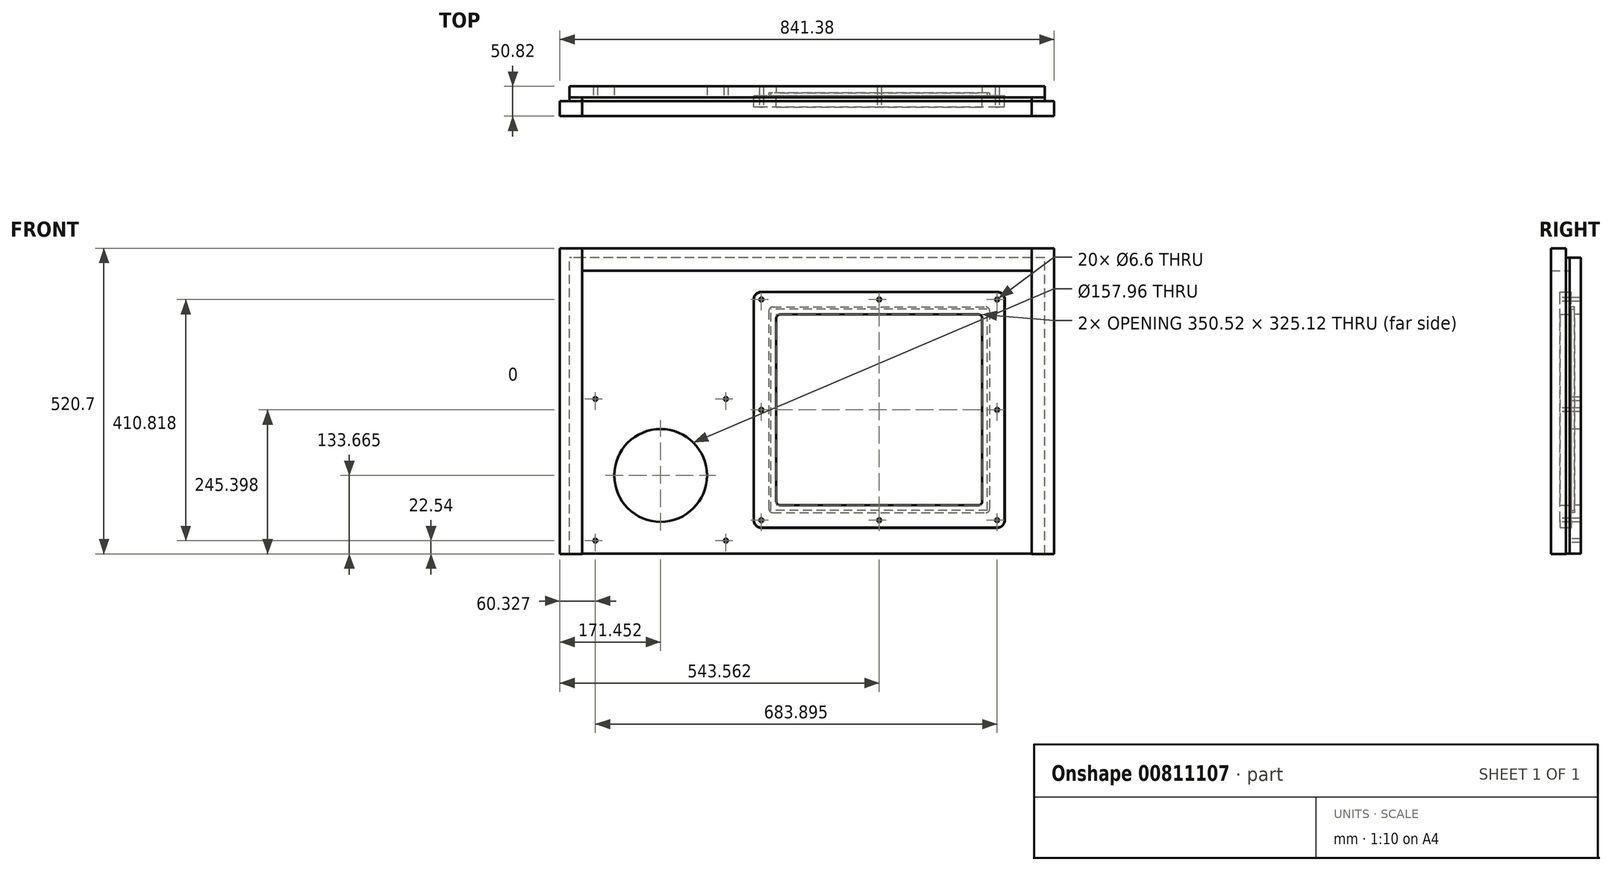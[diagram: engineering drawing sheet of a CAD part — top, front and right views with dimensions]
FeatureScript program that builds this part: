
annotation { "Feature Type Name" : "Feature", "Feature Type Description" : "" }
export const myFeature = defineFeature(function(context is Context, id is Id, definition is map)
    precondition{}
    {
        {
            var Q0;
            Q0=qCreatedBy(makeId("Front.planeOp"),FACE);
            cPlane(context, id + "F0", {"entities" : qUnion([Q0]), "cplaneType" : CPlaneType.OFFSET, "offset" : 25.4 * mm, "width" : 150 * mm, "height" : 150 * mm});
        }
        {
            var Q0;
            Q0=qCreatedBy(makeId("Front.planeOp"),FACE);
            var sketch = newSketch(context, id + "F1", { "sketchPlane" : qUnion([Q0])});
            skLineSegment(sketch, "E0.bottom", {"start": v(406.4, -254) * mm, "end": v(-406.4, -254) * mm});
            skLineSegment(sketch, "E0.top", {"start": v(406.4, 254) * mm, "end": v(-406.4, 254) * mm});
            skLineSegment(sketch, "E0.left", {"start": v(406.4, -254) * mm, "end": v(406.4, 254) * mm});
            skLineSegment(sketch, "E0.right", {"start": v(-406.4, -254) * mm, "end": v(-406.4, 254) * mm});
            skPoint(sketch, "E0.middle", {"position": v(0, 0) * mm});
            skSolve(sketch);
        }
        {
            var Q0;
            Q0=qCreatedBy(id+"F0.planeOp",FACE);
            var sketch = newSketch(context, id + "F2", { "sketchPlane" : qUnion([Q0])});
            skLineSegment(sketch, "E1.bottom", {"start": v(420.69, -252.41) * mm, "end": v(-420.69, -252.41) * mm});
            skLineSegment(sketch, "E1.top", {"start": v(420.69, 268.29) * mm, "end": v(-420.69, 268.29) * mm});
            skLineSegment(sketch, "E1.left", {"start": v(420.69, -252.41) * mm, "end": v(420.69, 268.29) * mm});
            skLineSegment(sketch, "E1.right", {"start": v(-420.69, -252.41) * mm, "end": v(-420.69, 268.29) * mm});
            skPoint(sketch, "E1.middle", {"position": v(0, 7.94) * mm});
            skSolve(sketch);
        }
        {
            var Q0;
            Q0=qCreatedBy(makeId("Front.planeOp"),FACE);
            var sketch = newSketch(context, id + "F3", { "sketchPlane" : qUnion([Q0])});
            skLineSegment(sketch, "E2.bottom", {"start": v(404.5, -252.1) * mm, "end": v(-404.5, -252.1) * mm});
            skLineSegment(sketch, "E2.top", {"start": v(404.5, 252.1) * mm, "end": v(-404.5, 252.1) * mm});
            skLineSegment(sketch, "E2.left", {"start": v(404.5, -252.1) * mm, "end": v(404.5, 252.1) * mm});
            skLineSegment(sketch, "E2.right", {"start": v(-404.5, -252.1) * mm, "end": v(-404.5, 252.1) * mm});
            skPoint(sketch, "E2.middle", {"position": v(0, 0) * mm});
            skLineSegment(sketch, "E3", {"start": v(-404.5, 22.52) * mm, "end": v(-406.4, 22.52) * mm, "construction": true});
            skLineSegment(sketch, "E4", {"start": v(-361.84, 252.1) * mm, "end": v(-361.84, 254) * mm, "construction": true});
            skSolve(sketch);
        }
        {
            var Q0;
            Q0 = qSketchRegion(id + "F3", true);
            extrude(context, id + "F4", {"entities" : qUnion([Q0]), "depth" : 19.05 * mm, "offsetDistance" : 25.4 * mm});
        }
        {
            var Q0;
            Q0=qCreatedBy(id+"F0.planeOp",FACE);
            var sketch = newSketch(context, id + "F5", { "sketchPlane" : qUnion([Q0])});
            skPoint(sketch, "E5", {"position": v(-420.69, 153.57) * mm});
            skLineSegment(sketch, "E6.bottom", {"start": v(-420.69, 268.29) * mm, "end": v(-382.59, 268.29) * mm});
            skLineSegment(sketch, "E6.top", {"start": v(-420.69, -252.41) * mm, "end": v(-382.59, -252.41) * mm});
            skLineSegment(sketch, "E6.left", {"start": v(-420.69, 268.29) * mm, "end": v(-420.69, -252.41) * mm});
            skLineSegment(sketch, "E6.right", {"start": v(-382.59, 268.29) * mm, "end": v(-382.59, -252.41) * mm});
            skLineSegment(sketch, "E7", {"start": v(0, 481.6) * mm, "end": v(0, -396.4) * mm, "construction": true});
            skLineSegment(sketch, "E8.MirrorCS", {"start": v(420.69, -252.41) * mm, "end": v(382.59, -252.41) * mm});
            skLineSegment(sketch, "E9.MirrorCS", {"start": v(382.59, 268.29) * mm, "end": v(382.59, -252.41) * mm});
            skLineSegment(sketch, "E10.MirrorCS", {"start": v(420.69, 268.29) * mm, "end": v(420.69, -252.41) * mm});
            skLineSegment(sketch, "E11.MirrorCS", {"start": v(420.69, 268.29) * mm, "end": v(382.59, 268.29) * mm});
            skPoint(sketch, "E12.MirrorP", {"position": v(420.69, 153.57) * mm});
            skLineSegment(sketch, "E13.bottom", {"start": v(-382.59, 268.29) * mm, "end": v(382.59, 268.29) * mm});
            skLineSegment(sketch, "E13.top", {"start": v(-382.59, 230.19) * mm, "end": v(382.59, 230.19) * mm});
            skLineSegment(sketch, "E13.left", {"start": v(-382.59, 268.29) * mm, "end": v(-382.59, 230.19) * mm});
            skLineSegment(sketch, "E13.right", {"start": v(382.59, 268.29) * mm, "end": v(382.59, 230.19) * mm});
            skSolve(sketch);
        }
        {
            var Q0;
            Q0=makeQuery(id+"F5.imprint","IMPRINT",FACE,{"disambiguationData":[TD([[makeQuery(id+"F5.imprint","IMPRINT",EDGE,{"derivedFrom":sQuery(id+"F5.wireOp",EDGE,"E6.bottom")}),-1.0]])]});
            var Q1;
            Q1=makeQuery(id+"F5.imprint","IMPRINT",FACE,{"disambiguationData":[TD([[makeQuery(id+"F5.imprint","IMPRINT",EDGE,{"derivedFrom":sQuery(id+"F5.wireOp",EDGE,"E8.MirrorCS")}),-1.0]])]});
            extrude(context, id + "F6", {"entities" : qUnion([Q0, Q1]), "depth" : 25.4 * mm + 5 / 203.2 * mm, "offsetDistance" : 25.4 * mm});
        }
        {
            var Q0;
            Q0=makeQuery(id+"F5.imprint","IMPRINT",FACE,{"disambiguationData":[TD([[makeQuery(id+"F5.imprint","IMPRINT",EDGE,{"derivedFrom":sQuery(id+"F5.wireOp",EDGE,"E13.bottom")}),-1.0]])]});
            var Q1;
            Q1=makeQuery(id+"F6.opExtrude","CAP_FACE",FACE,{"disambiguationData":[OSD([sQuery(id+"F5.wireOp",EDGE,"E6.bottom"),sQuery(id+"F5.wireOp",EDGE,"E6.top"),sQuery(id+"F5.wireOp",EDGE,"E6.left"),sQuery(id+"F5.wireOp",EDGE,"E6.right"),sQuery(id+"F5.wireOp",EDGE,"E13.left")])],"isStart":false});
            extrude(context, id + "F7", {"entities" : qUnion([Q0]), "endBound" : BoundingType.UP_TO_SURFACE, "depth" : 25.4 * mm, "endBoundEntityFace" : qUnion([Q1]), "offsetDistance" : 25.4 * mm});
        }
        {
            var Q0;
            Q0=makeQuery(id+"F4.opExtrude","CAP_FACE",FACE,{"disambiguationData":[OSD([sQuery(id+"F3.wireOp",EDGE,"E2.bottom"),sQuery(id+"F3.wireOp",EDGE,"E2.top"),sQuery(id+"F3.wireOp",EDGE,"E2.left"),sQuery(id+"F3.wireOp",EDGE,"E2.right")])],"isStart":false});
            var sketch = newSketch(context, id + "F8", { "sketchPlane" : qUnion([Q0])});
            skLineSegment(sketch, "E14.0", {"start": v(-404.5, -252.1) * mm, "end": v(-404.5, 252.1) * mm, "construction": true});
            skLineSegment(sketch, "E15.0", {"start": v(404.5, 252.1) * mm, "end": v(-404.5, 252.1) * mm, "construction": true});
            skLineSegment(sketch, "E16.0", {"start": v(404.5, -252.1) * mm, "end": v(404.5, 252.1) * mm, "construction": true});
            skLineSegment(sketch, "E17.0", {"start": v(420.69, -252.41) * mm, "end": v(382.59, -252.41) * mm, "construction": true});
            skLineSegment(sketch, "E18.0", {"start": v(382.59, 268.29) * mm, "end": v(382.59, -252.41) * mm, "construction": true});
            skLineSegment(sketch, "E19.0", {"start": v(-382.59, 268.29) * mm, "end": v(-382.59, -252.41) * mm, "construction": true});
            skLineSegment(sketch, "E20.0", {"start": v(-382.59, 230.19) * mm, "end": v(382.59, 230.19) * mm, "construction": true});
            skLineSegment(sketch, "E21.bottom", {"start": v(-404.5, 252.1) * mm, "end": v(-382.59, 252.1) * mm});
            skLineSegment(sketch, "E21.top", {"start": v(-404.5, -252.41) * mm, "end": v(-382.59, -252.41) * mm});
            skLineSegment(sketch, "E21.left", {"start": v(-404.5, 252.1) * mm, "end": v(-404.5, -252.41) * mm});
            skLineSegment(sketch, "E21.right", {"start": v(-382.59, 252.1) * mm, "end": v(-382.59, -252.41) * mm});
            skLineSegment(sketch, "E22.bottom", {"start": v(-382.59, 252.1) * mm, "end": v(382.59, 252.1) * mm});
            skLineSegment(sketch, "E22.top", {"start": v(-382.59, 230.19) * mm, "end": v(382.59, 230.19) * mm});
            skLineSegment(sketch, "E22.left", {"start": v(-382.59, 252.1) * mm, "end": v(-382.59, 230.19) * mm});
            skLineSegment(sketch, "E22.right", {"start": v(382.59, 252.1) * mm, "end": v(382.59, 230.19) * mm});
            skLineSegment(sketch, "E23.bottom", {"start": v(382.59, 252.1) * mm, "end": v(404.5, 252.1) * mm});
            skLineSegment(sketch, "E23.top", {"start": v(382.59, -252.1) * mm, "end": v(404.5, -252.1) * mm});
            skLineSegment(sketch, "E23.left", {"start": v(382.59, 252.1) * mm, "end": v(382.59, -252.1) * mm});
            skLineSegment(sketch, "E23.right", {"start": v(404.5, 252.1) * mm, "end": v(404.5, -252.1) * mm});
            skSolve(sketch);
        }
        {
            var Q0;
            Q0=makeQuery(id+"F8.imprint","IMPRINT",FACE,{"disambiguationData":[TD([[makeQuery(id+"F8.imprint","IMPRINT",EDGE,{"derivedFrom":sQuery(id+"F8.wireOp",EDGE,"E21.bottom")}),1.0]])]});
            var Q1;
            {var subQ3=sQuery(id+"F8.wireOp",EDGE,"E23.bottom");Q1=makeQuery(id+"F8.imprint","IMPRINT",FACE,{"disambiguationData":[TD([[makeQuery(id+"F8.imprint","IMPRINT",EDGE,{"derivedFrom":subQ3}),1.0]])]});}
            var Q2;
            Q2=qCreatedBy(id+"F0.planeOp",FACE);
            extrude(context, id + "F9", {"entities" : qUnion([Q0, Q1]), "endBound" : BoundingType.UP_TO_SURFACE, "depth" : 25.4 * mm, "endBoundEntityFace" : qUnion([Q2]), "offsetDistance" : 25.4 * mm});
        }
        {
            var Q0;
            {var subQ0=sQuery(id+"F8.wireOp",EDGE,"E22.bottom");Q0=makeQuery(id+"F8.imprint","IMPRINT",FACE,{"disambiguationData":[TD([[makeQuery(id+"F8.imprint","IMPRINT",EDGE,{"derivedFrom":subQ0}),1.0]])]});}
            var Q1;
            Q1=qCreatedBy(id+"F0.planeOp",FACE);
            extrude(context, id + "F10", {"entities" : qUnion([Q0]), "endBound" : BoundingType.UP_TO_SURFACE, "depth" : 25.4 * mm, "endBoundEntityFace" : qUnion([Q1]), "offsetDistance" : 25.4 * mm});
        }
        {
            var Q0;
            Q0=makeQuery(id+"F4.opExtrude","CAP_FACE",FACE,{"disambiguationData":[OSD([sQuery(id+"F3.wireOp",EDGE,"E2.bottom"),sQuery(id+"F3.wireOp",EDGE,"E2.top"),sQuery(id+"F3.wireOp",EDGE,"E2.left"),sQuery(id+"F3.wireOp",EDGE,"E2.right")])],"isStart":false});
            var sketch = newSketch(context, id + "F11", { "sketchPlane" : qUnion([Q0])});
            skLineSegment(sketch, "E24", {"start": v(-638.96, -118.75) * mm, "end": v(167.87, -118.75) * mm, "construction": true});
            skLineSegment(sketch, "E25", {"start": v(-249.24, -343.57) * mm, "end": v(-249.24, 396.02) * mm, "construction": true});
            skCircle(sketch, "E26", {"center": v(-249.24, -118.75) * mm, "radius": 77.79 * mm, "construction": true});
            skLineSegment(sketch, "E27.bottom", {"start": v(-369.89, 20.95) * mm, "end": v(-128.59, 20.95) * mm, "construction": true});
            skLineSegment(sketch, "E27.top", {"start": v(-369.89, -239.4) * mm, "end": v(-128.59, -239.4) * mm, "construction": true});
            skLineSegment(sketch, "E27.left", {"start": v(-369.89, 20.95) * mm, "end": v(-369.89, -239.4) * mm, "construction": true});
            skLineSegment(sketch, "E27.right", {"start": v(-128.59, 20.95) * mm, "end": v(-128.59, -239.4) * mm, "construction": true});
            skPoint(sketch, "E28", {"position": v(-249.24, 20.95) * mm});
            skLineSegment(sketch, "E29", {"start": v(-360.36, 91.16) * mm, "end": v(-360.36, -269.14) * mm, "construction": true});
            skLineSegment(sketch, "E30", {"start": v(-374.2, 11.43) * mm, "end": v(-35.6, 11.43) * mm, "construction": true});
            skLineSegment(sketch, "E31", {"start": v(-377.42, -229.87) * mm, "end": v(-85.49, -229.87) * mm, "construction": true});
            skCircle(sketch, "E32", {"center": v(-360.36, -229.87) * mm, "radius": 3.3 * mm});
            skCircle(sketch, "E33", {"center": v(-360.36, 11.43) * mm, "radius": 3.3 * mm});
            skCircle(sketch, "E34.MirrorC", {"center": v(-138.11, -229.87) * mm, "radius": 3.3 * mm});
            skCircle(sketch, "E35.MirrorC", {"center": v(-138.11, 11.43) * mm, "radius": 3.3 * mm});
            skCircle(sketch, "E36", {"center": v(-249.24, -118.75) * mm, "radius": 78.98 * mm});
            skLineSegment(sketch, "E37", {"start": v(-249.24, -118.75) * mm, "end": v(-193.1, -64.9) * mm, "construction": true});
            skLineSegment(sketch, "E38", {"start": v(-193.1, -64.9) * mm, "end": v(-192.24, -64.08) * mm, "construction": true});
            skSolve(sketch);
        }
        {
            var Q0;
            Q0 = qSketchRegion(id + "F11", true);
            extrude(context, id + "F12", {"entities" : qUnion([Q0]), "operationType" : NewBodyOperationType.REMOVE, "endBound" : BoundingType.THROUGH_ALL, "oppositeDirection" : true, "depth" : 25.4 * mm, "offsetDistance" : 25.4 * mm});
        }
        {
            var Q0;
            Q0=makeQuery(id+"F11.imprint","IMPRINT",FACE,{"disambiguationData":[TD([[makeQuery(id+"F11.imprint","IMPRINT",EDGE,{"derivedFrom":sQuery(id+"F11.wireOp",EDGE,"E32")}),-1.0]])]});
            var sketch = newSketch(context, id + "F13", { "sketchPlane" : qUnion([Q0])});
            skLineSegment(sketch, "E39.bottom", {"start": v(304.36, -182.27) * mm, "end": v(-58.61, -182.27) * mm});
            skLineSegment(sketch, "E39.top", {"start": v(304.36, 168.25) * mm, "end": v(-58.61, 168.25) * mm});
            skLineSegment(sketch, "E39.left", {"start": v(310.83, -175.8) * mm, "end": v(310.83, 161.77) * mm});
            skLineSegment(sketch, "E39.right", {"start": v(-65.09, -175.8) * mm, "end": v(-65.09, 161.77) * mm});
            skPoint(sketch, "E39.middle", {"position": v(122.87, -7.01) * mm});
            skPoint(sketch, "E40.visualSharp", {"position": v(-65.09, 168.25) * mm});
            skArc(sketch, "E40.filletArc", {"start": v(-58.61, 168.25) * mm, "mid": v(-63.2, 166.35) * mm, "end": v(-65.09, 161.77) * mm});
            skPoint(sketch, "E41.visualSharp", {"position": v(310.83, 168.25) * mm});
            skArc(sketch, "E41.filletArc", {"start": v(310.83, 161.77) * mm, "mid": v(308.94, 166.35) * mm, "end": v(304.36, 168.25) * mm});
            skPoint(sketch, "E42.visualSharp", {"position": v(310.83, -182.27) * mm});
            skArc(sketch, "E42.filletArc", {"start": v(304.36, -182.27) * mm, "mid": v(308.94, -180.38) * mm, "end": v(310.83, -175.8) * mm});
            skPoint(sketch, "E43.visualSharp", {"position": v(-65.09, -182.27) * mm});
            skArc(sketch, "E43.filletArc", {"start": v(-65.09, -175.8) * mm, "mid": v(-63.2, -180.38) * mm, "end": v(-58.61, -182.27) * mm});
            skLineSegment(sketch, "E44.bottom", {"start": v(307.02, -178.46) * mm, "end": v(-61.28, -178.46) * mm});
            skLineSegment(sketch, "E44.top", {"start": v(307.02, 164.44) * mm, "end": v(-61.28, 164.44) * mm});
            skLineSegment(sketch, "E44.left", {"start": v(307.02, -178.46) * mm, "end": v(307.02, 164.44) * mm});
            skLineSegment(sketch, "E44.right", {"start": v(-61.28, -178.46) * mm, "end": v(-61.28, 164.44) * mm});
            skLineSegment(sketch, "E45", {"start": v(-65.09, 100.23) * mm, "end": v(-61.28, 100.23) * mm, "construction": true});
            skLineSegment(sketch, "E46", {"start": v(142.05, 164.44) * mm, "end": v(142.05, 168.25) * mm, "construction": true});
            skLineSegment(sketch, "E47.0", {"start": v(-52.39, -163.1) * mm, "end": v(-52.39, 149.07) * mm});
            skLineSegment(sketch, "E47.1", {"start": v(291.66, -169.57) * mm, "end": v(-45.91, -169.57) * mm});
            skLineSegment(sketch, "E47.2", {"start": v(298.13, -163.1) * mm, "end": v(298.13, 149.07) * mm});
            skLineSegment(sketch, "E47.3", {"start": v(291.66, 155.55) * mm, "end": v(-45.91, 155.55) * mm});
            skPoint(sketch, "E48.visualSharp", {"position": v(-52.39, 155.55) * mm});
            skArc(sketch, "E48.filletArc", {"start": v(-45.91, 155.55) * mm, "mid": v(-50.5, 153.65) * mm, "end": v(-52.39, 149.07) * mm});
            skPoint(sketch, "E49.visualSharp", {"position": v(298.13, 155.55) * mm});
            skArc(sketch, "E49.filletArc", {"start": v(298.13, 149.07) * mm, "mid": v(296.24, 153.65) * mm, "end": v(291.66, 155.55) * mm});
            skPoint(sketch, "E50.visualSharp", {"position": v(298.13, -169.57) * mm});
            skArc(sketch, "E50.filletArc", {"start": v(291.66, -169.57) * mm, "mid": v(296.24, -167.68) * mm, "end": v(298.13, -163.1) * mm});
            skPoint(sketch, "E51.visualSharp", {"position": v(-52.39, -169.57) * mm});
            skArc(sketch, "E51.filletArc", {"start": v(-52.39, -163.1) * mm, "mid": v(-50.5, -167.68) * mm, "end": v(-45.91, -169.57) * mm});
            skSolve(sketch);
        }
        {
            var Q0;
            Q0=makeQuery(id+"F13.imprint","IMPRINT",FACE,{"disambiguationData":[TD([[makeQuery(id+"F13.imprint","IMPRINT",EDGE,{"derivedFrom":sQuery(id+"F13.wireOp",EDGE,"E47.0")}),-1.0]])]});
            extrude(context, id + "F14", {"entities" : qUnion([Q0]), "operationType" : NewBodyOperationType.REMOVE, "endBound" : BoundingType.THROUGH_ALL, "oppositeDirection" : true, "depth" : 25.4 * mm, "offsetDistance" : 25.4 * mm});
        }
        {
            var Q0;
            Q0=makeQuery(id+"F13.imprint","IMPRINT",FACE,{"disambiguationData":[TD([[makeQuery(id+"F13.imprint","IMPRINT",EDGE,{"derivedFrom":sQuery(id+"F13.wireOp",EDGE,"E39.bottom")}),-1.0]])]});
            var Q1;
            Q1=makeQuery(id+"F13.imprint","IMPRINT",FACE,{"disambiguationData":[TD([[makeQuery(id+"F13.imprint","IMPRINT",EDGE,{"derivedFrom":sQuery(id+"F13.wireOp",EDGE,"E44.bottom")}),-1.0]])]});
            var Q2;
            Q2=makeQuery(id+"F13.imprint","IMPRINT",FACE,{"disambiguationData":[TD([[makeQuery(id+"F13.imprint","IMPRINT",EDGE,{"derivedFrom":sQuery(id+"F13.wireOp",EDGE,"E47.0")}),-1.0]])]});
            extrude(context, id + "F15", {"entities" : qUnion([Q0, Q1, Q2]), "operationType" : NewBodyOperationType.REMOVE, "oppositeDirection" : true, "depth" : 5.6 * mm + 2.54 * mm, "offsetDistance" : 25.4 * mm});
        }
        {
            var Q0;
            Q0=makeQuery(id+"F15.boolean.opBoolean","COPY",FACE,{"derivedFrom":makeQuery(id+"F15.opExtrude","CAP_FACE",FACE,{"disambiguationData":[OSD([sQuery(id+"F13.wireOp",EDGE,"E39.bottom"),sQuery(id+"F13.wireOp",EDGE,"E39.top"),sQuery(id+"F13.wireOp",EDGE,"E39.left"),sQuery(id+"F13.wireOp",EDGE,"E39.right"),sQuery(id+"F13.wireOp",EDGE,"E40.filletArc"),sQuery(id+"F13.wireOp",EDGE,"E41.filletArc"),sQuery(id+"F13.wireOp",EDGE,"E42.filletArc"),sQuery(id+"F13.wireOp",EDGE,"E43.filletArc")])],"isStart":false})});
            var sketch = newSketch(context, id + "F16", { "sketchPlane" : qUnion([Q0])});
            skLineSegment(sketch, "E52.0", {"start": v(307.02, -178.46) * mm, "end": v(-61.28, -178.46) * mm});
            skLineSegment(sketch, "E53.0", {"start": v(-61.28, -178.46) * mm, "end": v(-61.28, 164.44) * mm});
            skLineSegment(sketch, "E54.0", {"start": v(307.02, -178.46) * mm, "end": v(307.02, 164.44) * mm});
            skLineSegment(sketch, "E55.0", {"start": v(307.02, 164.44) * mm, "end": v(-61.28, 164.44) * mm});
            skSolve(sketch);
        }
        {
            var Q0;
            Q0 = qSketchRegion(id + "F16", true);
            extrude(context, id + "F17", {"entities" : qUnion([Q0]), "depth" : 5.6 * mm, "offsetDistance" : 25.4 * mm});
        }
        {
            var Q0;
            Q0=makeQuery(id+"F13.imprint","IMPRINT",FACE,{"disambiguationData":[TD([[makeQuery(id+"F13.imprint","IMPRINT",EDGE,{"derivedFrom":sQuery(id+"F13.wireOp",EDGE,"E39.bottom")}),1.0]])]});
            var sketch = newSketch(context, id + "F18", { "sketchPlane" : qUnion([Q0])});
            skLineSegment(sketch, "E56.bottom", {"start": v(323.53, -207.67) * mm, "end": v(-77.79, -207.67) * mm});
            skLineSegment(sketch, "E56.top", {"start": v(323.53, 193.65) * mm, "end": v(-77.79, 193.65) * mm});
            skLineSegment(sketch, "E56.left", {"start": v(336.23, -194.97) * mm, "end": v(336.23, 180.95) * mm});
            skLineSegment(sketch, "E56.right", {"start": v(-90.49, -194.97) * mm, "end": v(-90.49, 180.95) * mm});
            skPoint(sketch, "E56.middle", {"position": v(122.87, -7.01) * mm});
            skArc(sketch, "E57.0.0", {"start": v(291.66, -169.57) * mm, "mid": v(296.24, -167.68) * mm, "end": v(298.13, -163.1) * mm});
            skLineSegment(sketch, "E57.0.1", {"start": v(298.13, -163.1) * mm, "end": v(298.13, 149.07) * mm});
            skArc(sketch, "E57.0.2", {"start": v(298.13, 149.07) * mm, "mid": v(296.24, 153.65) * mm, "end": v(291.66, 155.55) * mm});
            skLineSegment(sketch, "E57.0.3", {"start": v(291.66, 155.55) * mm, "end": v(-45.91, 155.55) * mm});
            skArc(sketch, "E57.0.4", {"start": v(-45.91, 155.55) * mm, "mid": v(-50.5, 153.65) * mm, "end": v(-52.39, 149.07) * mm});
            skLineSegment(sketch, "E57.0.5", {"start": v(-52.39, 149.07) * mm, "end": v(-52.39, -163.1) * mm});
            skArc(sketch, "E57.0.6", {"start": v(-52.39, -163.1) * mm, "mid": v(-50.5, -167.68) * mm, "end": v(-45.91, -169.57) * mm});
            skLineSegment(sketch, "E57.0.7", {"start": v(-45.91, -169.57) * mm, "end": v(291.66, -169.57) * mm});
            skPoint(sketch, "E58.visualSharp", {"position": v(-90.49, 193.65) * mm});
            skArc(sketch, "E58.filletArc", {"start": v(-77.79, 193.65) * mm, "mid": v(-86.77, 189.93) * mm, "end": v(-90.49, 180.95) * mm});
            skPoint(sketch, "E59.visualSharp", {"position": v(336.23, 193.65) * mm});
            skArc(sketch, "E59.filletArc", {"start": v(336.23, 180.95) * mm, "mid": v(332.51, 189.93) * mm, "end": v(323.53, 193.65) * mm});
            skPoint(sketch, "E60.visualSharp", {"position": v(336.23, -207.67) * mm});
            skArc(sketch, "E60.filletArc", {"start": v(323.53, -207.67) * mm, "mid": v(332.51, -203.95) * mm, "end": v(336.23, -194.97) * mm});
            skPoint(sketch, "E61.visualSharp", {"position": v(-90.49, -207.67) * mm});
            skArc(sketch, "E61.filletArc", {"start": v(-90.49, -194.97) * mm, "mid": v(-86.77, -203.95) * mm, "end": v(-77.79, -207.67) * mm});
            skPoint(sketch, "E62", {"position": v(-77.79, -7.01) * mm});
            skPoint(sketch, "E63", {"position": v(122.87, 180.95) * mm});
            skPoint(sketch, "E64", {"position": v(122.87, -194.97) * mm});
            skPoint(sketch, "E65", {"position": v(122.87, 193.65) * mm});
            skPoint(sketch, "E66", {"position": v(-90.49, -7.01) * mm});
            skPoint(sketch, "E67", {"position": v(122.87, -207.67) * mm});
            skPoint(sketch, "E68", {"position": v(122.87, 168.25) * mm});
            skPoint(sketch, "E69", {"position": v(-65.09, -7.01) * mm});
            skPoint(sketch, "E70", {"position": v(122.87, -182.27) * mm});
            skLineSegment(sketch, "E71", {"start": v(122.87, 227.82) * mm, "end": v(122.87, -239.42) * mm, "construction": true});
            skPoint(sketch, "E72", {"position": v(-77.79, -101) * mm});
            skPoint(sketch, "E73", {"position": v(-77.79, 86.97) * mm});
            skPoint(sketch, "E74", {"position": v(22.54, 180.95) * mm});
            skPoint(sketch, "E75", {"position": v(22.54, -194.97) * mm});
            skPoint(sketch, "E76.MirrorP", {"position": v(223.2, 180.95) * mm});
            skPoint(sketch, "E77.MirrorP", {"position": v(323.53, 86.97) * mm});
            skPoint(sketch, "E78.MirrorP", {"position": v(323.53, -7.01) * mm});
            skPoint(sketch, "E79.MirrorP", {"position": v(323.53, -101) * mm});
            skPoint(sketch, "E80.MirrorP", {"position": v(223.2, -194.97) * mm});
            skSolve(sketch);
        }
        {
            var Q0;
            Q0 = qSketchRegion(id + "F18", true);
            extrude(context, id + "F19", {"entities" : qUnion([Q0]), "depth" : 19.05 * mm, "offsetDistance" : 25.4 * mm});
        }
        {
            var Q0;
            Q0=makeQuery(id+"F19.opExtrude","SWEPT_BODY",BODY,{"disambiguationData":[OSD([sQuery(id+"F18.wireOp",EDGE,"E56.bottom"),sQuery(id+"F18.wireOp",EDGE,"E56.top"),sQuery(id+"F18.wireOp",EDGE,"E56.left"),sQuery(id+"F18.wireOp",EDGE,"E56.right"),sQuery(id+"F18.wireOp",EDGE,"E57.0.0"),sQuery(id+"F18.wireOp",EDGE,"E57.0.1"),sQuery(id+"F18.wireOp",EDGE,"E57.0.2"),sQuery(id+"F18.wireOp",EDGE,"E57.0.3"),sQuery(id+"F18.wireOp",EDGE,"E57.0.4"),sQuery(id+"F18.wireOp",EDGE,"E57.0.5"),sQuery(id+"F18.wireOp",EDGE,"E57.0.6"),sQuery(id+"F18.wireOp",EDGE,"E57.0.7"),sQuery(id+"F18.wireOp",EDGE,"E58.filletArc"),sQuery(id+"F18.wireOp",EDGE,"E59.filletArc"),sQuery(id+"F18.wireOp",EDGE,"E60.filletArc"),sQuery(id+"F18.wireOp",EDGE,"E61.filletArc")])]});
            var Q1;
            Q1=makeQuery(id+"F19.opExtrude","SWEPT_EDGE",EDGE,{"disambiguationData":[OSD([sQuery(id+"F18.wireOp",EDGE,"E56.right"),sQuery(id+"F18.wireOp",EDGE,"E61.filletArc")])]});
            transform(context, id + "F20", {"entities" : qUnion([Q0]), "transformType" : TransformType.TRANSLATION_DISTANCE, "transformDirection" : qUnion([Q1]), "distance" : 2.54 * mm, "makeCopy" : false});
        }
        {
            var Q0;
            Q0=makeQuery(id+"F19.opExtrude","SWEPT_BODY",BODY,{"disambiguationData":[OSD([sQuery(id+"F18.wireOp",EDGE,"E56.bottom"),sQuery(id+"F18.wireOp",EDGE,"E56.top"),sQuery(id+"F18.wireOp",EDGE,"E56.left"),sQuery(id+"F18.wireOp",EDGE,"E56.right"),sQuery(id+"F18.wireOp",EDGE,"E57.0.0"),sQuery(id+"F18.wireOp",EDGE,"E57.0.1"),sQuery(id+"F18.wireOp",EDGE,"E57.0.2"),sQuery(id+"F18.wireOp",EDGE,"E57.0.3"),sQuery(id+"F18.wireOp",EDGE,"E57.0.4"),sQuery(id+"F18.wireOp",EDGE,"E57.0.5"),sQuery(id+"F18.wireOp",EDGE,"E57.0.6"),sQuery(id+"F18.wireOp",EDGE,"E57.0.7"),sQuery(id+"F18.wireOp",EDGE,"E58.filletArc"),sQuery(id+"F18.wireOp",EDGE,"E59.filletArc"),sQuery(id+"F18.wireOp",EDGE,"E60.filletArc"),sQuery(id+"F18.wireOp",EDGE,"E61.filletArc")])]});
            var Q1;
            Q1=makeQuery(id+"F4.opExtrude","SWEPT_BODY",BODY,{"disambiguationData":[OSD([sQuery(id+"F3.wireOp",EDGE,"E2.bottom"),sQuery(id+"F3.wireOp",EDGE,"E2.top"),sQuery(id+"F3.wireOp",EDGE,"E2.left"),sQuery(id+"F3.wireOp",EDGE,"E2.right")])]});
            var Q2;
            Q2=makeQuery(id+"F19.opExtrude","SWEPT_FACE",FACE,{"disambiguationData":[OSD([sQuery(id+"F18.wireOp",EDGE,"E56.right")])]});
            var Q3;
            Q3=makeQuery(id+"F19.opExtrude","SWEPT_FACE",FACE,{"disambiguationData":[OSD([sQuery(id+"F18.wireOp",EDGE,"E61.filletArc")])]});
            var Q4;
            Q4=makeQuery(id+"F19.opExtrude","SWEPT_FACE",FACE,{"disambiguationData":[OSD([sQuery(id+"F18.wireOp",EDGE,"E56.bottom")])]});
            var Q5;
            Q5=makeQuery(id+"F19.opExtrude","SWEPT_FACE",FACE,{"disambiguationData":[OSD([sQuery(id+"F18.wireOp",EDGE,"E60.filletArc")])]});
            var Q6;
            Q6=makeQuery(id+"F19.opExtrude","SWEPT_FACE",FACE,{"disambiguationData":[OSD([sQuery(id+"F18.wireOp",EDGE,"E56.left")])]});
            var Q7;
            Q7=makeQuery(id+"F19.opExtrude","SWEPT_FACE",FACE,{"disambiguationData":[OSD([sQuery(id+"F18.wireOp",EDGE,"E59.filletArc")])]});
            var Q8;
            Q8=makeQuery(id+"F19.opExtrude","SWEPT_FACE",FACE,{"disambiguationData":[OSD([sQuery(id+"F18.wireOp",EDGE,"E56.top")])]});
            var Q9;
            Q9=makeQuery(id+"F19.opExtrude","SWEPT_FACE",FACE,{"disambiguationData":[OSD([sQuery(id+"F18.wireOp",EDGE,"E58.filletArc")])]});
            booleanBodies(context, id + "F21", {"operationType" : BooleanOperationType.SUBTRACTION, "tools" : qUnion([Q0]), "targets" : qUnion([Q1]), "offset" : true, "entitiesToOffset" : qUnion([Q2, Q3, Q4, Q5, Q6, Q7, Q8, Q9]), "offsetDistance" : .35 * mm, "keepTools" : true});
        }
        {
            var Q0;
            Q0=makeQuery(id+"F19.opExtrude","CAP_FACE",FACE,{"disambiguationData":[OSD([sQuery(id+"F18.wireOp",EDGE,"E56.bottom"),sQuery(id+"F18.wireOp",EDGE,"E56.top"),sQuery(id+"F18.wireOp",EDGE,"E56.left"),sQuery(id+"F18.wireOp",EDGE,"E56.right"),sQuery(id+"F18.wireOp",EDGE,"E57.0.0"),sQuery(id+"F18.wireOp",EDGE,"E57.0.1"),sQuery(id+"F18.wireOp",EDGE,"E57.0.2"),sQuery(id+"F18.wireOp",EDGE,"E57.0.3"),sQuery(id+"F18.wireOp",EDGE,"E57.0.4"),sQuery(id+"F18.wireOp",EDGE,"E57.0.5"),sQuery(id+"F18.wireOp",EDGE,"E57.0.6"),sQuery(id+"F18.wireOp",EDGE,"E57.0.7"),sQuery(id+"F18.wireOp",EDGE,"E58.filletArc"),sQuery(id+"F18.wireOp",EDGE,"E59.filletArc"),sQuery(id+"F18.wireOp",EDGE,"E60.filletArc"),sQuery(id+"F18.wireOp",EDGE,"E61.filletArc")])],"isStart":false});
            var sketch = newSketch(context, id + "F22", { "sketchPlane" : qUnion([Q0])});
            skPoint(sketch, "E81.0", {"position": v(22.54, -194.97) * mm});
            skPoint(sketch, "E82.0", {"position": v(-77.79, -194.97) * mm});
            skPoint(sketch, "E83.0", {"position": v(-77.79, -101) * mm});
            skPoint(sketch, "E84.0", {"position": v(-77.79, -7.01) * mm});
            skPoint(sketch, "E85.0", {"position": v(-77.79, 86.97) * mm});
            skPoint(sketch, "E86.0", {"position": v(-77.79, 180.95) * mm});
            skPoint(sketch, "E87.0", {"position": v(22.54, 180.95) * mm});
            skPoint(sketch, "E88.0", {"position": v(122.87, 180.95) * mm});
            skPoint(sketch, "E89.0", {"position": v(223.2, 180.95) * mm});
            skPoint(sketch, "E90.0", {"position": v(323.53, 180.95) * mm});
            skPoint(sketch, "E91.0", {"position": v(323.53, 86.97) * mm});
            skPoint(sketch, "E92.0", {"position": v(323.53, -7.01) * mm});
            skPoint(sketch, "E93.0", {"position": v(323.53, -101) * mm});
            skPoint(sketch, "E94.0", {"position": v(323.53, -194.97) * mm});
            skPoint(sketch, "E95.0", {"position": v(223.2, -194.97) * mm});
            skPoint(sketch, "E96.0", {"position": v(122.87, -194.97) * mm});
            skSolve(sketch);
        }
        {
            var Q0;
            Q0=sQuery(id+"F22.wireOp",VERTEX,"E88.0");
            var Q1;
            Q1=sQuery(id+"F22.wireOp",VERTEX,"E90.0");
            var Q2;
            Q2=sQuery(id+"F22.wireOp",VERTEX,"E92.0");
            var Q3;
            Q3=sQuery(id+"F22.wireOp",VERTEX,"E94.0");
            var Q4;
            Q4=sQuery(id+"F22.wireOp",VERTEX,"E96.0");
            var Q5;
            Q5=sQuery(id+"F22.wireOp",VERTEX,"E82.0");
            var Q6;
            Q6=sQuery(id+"F22.wireOp",VERTEX,"E84.0");
            var Q7;
            Q7=sQuery(id+"F22.wireOp",VERTEX,"E86.0");
            var Q8;
            Q8=makeQuery(id+"F19.opExtrude","SWEPT_BODY",BODY,{"disambiguationData":[OSD([sQuery(id+"F18.wireOp",EDGE,"E56.bottom"),sQuery(id+"F18.wireOp",EDGE,"E56.top"),sQuery(id+"F18.wireOp",EDGE,"E56.left"),sQuery(id+"F18.wireOp",EDGE,"E56.right"),sQuery(id+"F18.wireOp",EDGE,"E57.0.0"),sQuery(id+"F18.wireOp",EDGE,"E57.0.1"),sQuery(id+"F18.wireOp",EDGE,"E57.0.2"),sQuery(id+"F18.wireOp",EDGE,"E57.0.3"),sQuery(id+"F18.wireOp",EDGE,"E57.0.4"),sQuery(id+"F18.wireOp",EDGE,"E57.0.5"),sQuery(id+"F18.wireOp",EDGE,"E57.0.6"),sQuery(id+"F18.wireOp",EDGE,"E57.0.7"),sQuery(id+"F18.wireOp",EDGE,"E58.filletArc"),sQuery(id+"F18.wireOp",EDGE,"E59.filletArc"),sQuery(id+"F18.wireOp",EDGE,"E60.filletArc"),sQuery(id+"F18.wireOp",EDGE,"E61.filletArc")])]});
            var Q9;
            Q9=makeQuery(id+"F4.opExtrude","SWEPT_BODY",BODY,{"disambiguationData":[OSD([sQuery(id+"F3.wireOp",EDGE,"E2.bottom"),sQuery(id+"F3.wireOp",EDGE,"E2.top"),sQuery(id+"F3.wireOp",EDGE,"E2.left"),sQuery(id+"F3.wireOp",EDGE,"E2.right")])]});
            hole(context, id + "F23", {"style" : HoleStyle.SIMPLE, "endStyle" : HoleEndStyle.THROUGH, "holeDiameter" : 6.6 * mm, "majorDiameter" : 6.35 * mm, "isTappedThrough" : true, "tappedDepth" : 12.7 * mm, "tapClearance" : 3, "locations" : qUnion([Q0, Q1, Q2, Q3, Q4, Q5, Q6, Q7]), "scope" : qUnion([Q8, Q9])});
        }
    });
